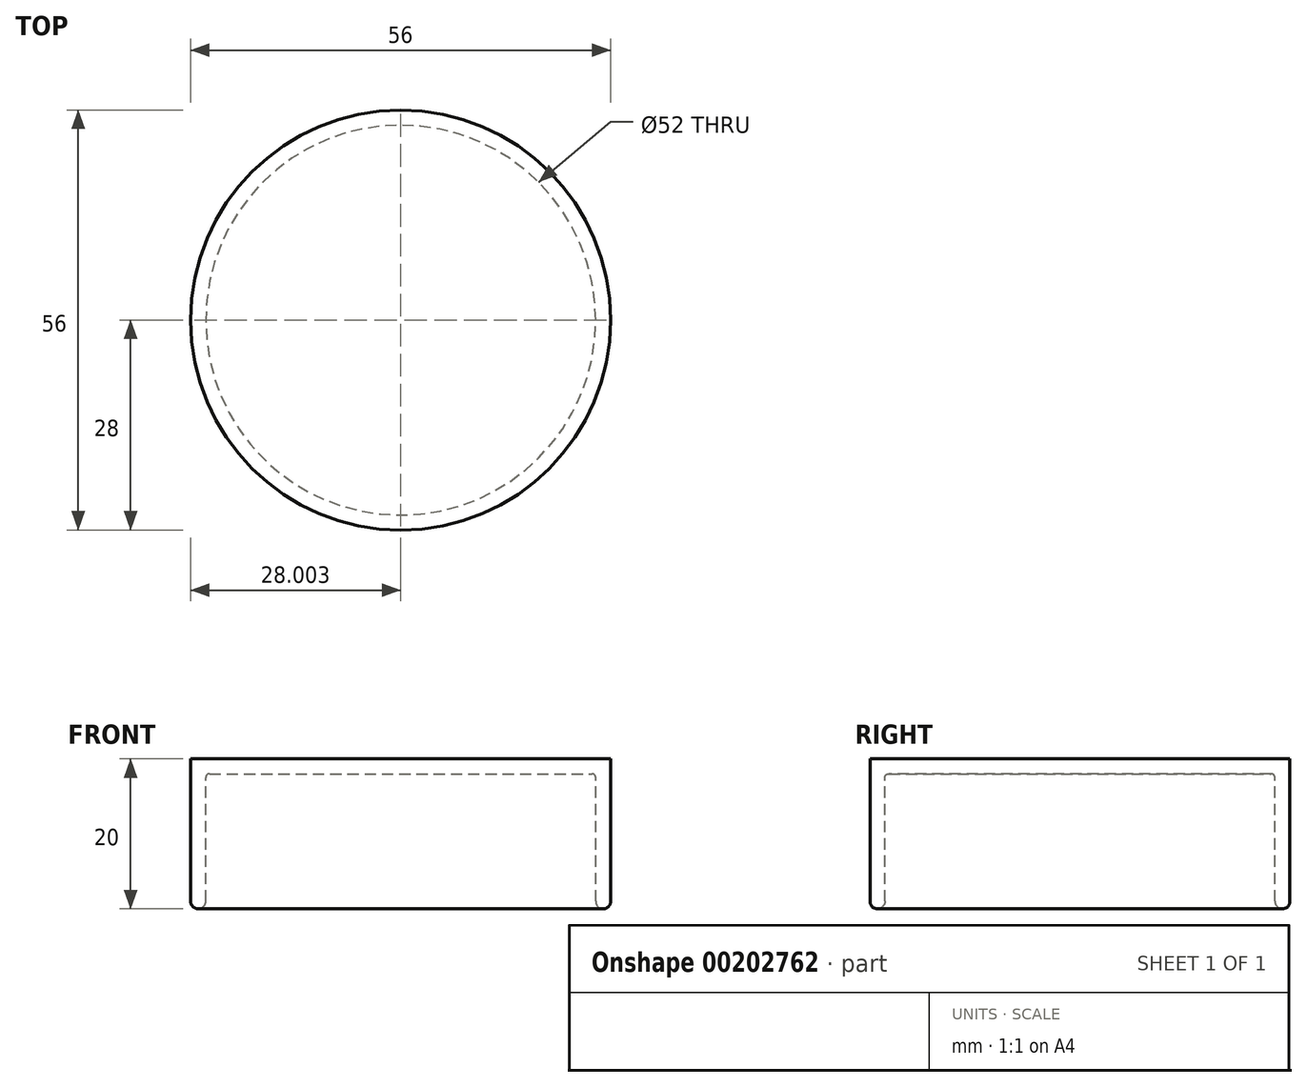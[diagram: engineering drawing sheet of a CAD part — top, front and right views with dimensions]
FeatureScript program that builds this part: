
annotation { "Feature Type Name" : "Feature", "Feature Type Description" : "" }
export const myFeature = defineFeature(function(context is Context, id is Id, definition is map)
    precondition{}
    {
        {
            var Q0;
            Q0=qCreatedBy(makeId("Front.planeOp"),FACE);
            var sketch = newSketch(context, id + "F0", { "sketchPlane" : qUnion([Q0])});
            skLineSegment(sketch, "E0.bottom", {"start": v(-8.82, 16.52) * mm, "end": v(19.18, 16.52) * mm});
            skLineSegment(sketch, "E0.top", {"start": v(-8.82, -3.48) * mm, "end": v(-6.82, -3.48) * mm});
            skLineSegment(sketch, "E0.left", {"start": v(-8.82, 16.52) * mm, "end": v(-8.82, -3.48) * mm});
            skLineSegment(sketch, "E0.right", {"start": v(19.18, 16.52) * mm, "end": v(19.18, 14.52) * mm});
            skLineSegment(sketch, "E1.0", {"start": v(-6.82, 14.52) * mm, "end": v(19.18, 14.52) * mm});
            skLineSegment(sketch, "E1.1", {"start": v(-6.82, 14.52) * mm, "end": v(-6.82, -3.48) * mm});
            skSolve(sketch);
        }
        {
            var Q0;
            Q0=makeQuery(id+"F0.imprint","IMPRINT",FACE,{"disambiguationData":[TD([[makeQuery(id+"F0.imprint","IMPRINT",EDGE,{"derivedFrom":sQuery(id+"F0.wireOp",EDGE,"E0.bottom")}),-1.0]])]});
            var Q1;
            Q1=sQuery(id+"F0.wireOp",EDGE,"E0.right");
            revolve(context, id + "F1", {"entities" : qUnion([Q0]), "axis" : qUnion([Q1]), "revolveType" : RevolveType.FULL});
        }
        {
            var Q0;
            Q0=makeQuery(id+"F1.opRevolve","SWEPT_FACE",FACE,{"disambiguationData":[OSD([sQuery(id+"F0.wireOp",EDGE,"E0.top")])]});
            fillet(context, id + "F2", {"entities" : qUnion([Q0]), "radius" : 1 * mm, "tangentPropagation" : true, "allowEdgeOverflow" : false});
        }
        {
            var Q0;
            Q0=makeQuery(id+"F1.opRevolve","SWEPT_EDGE",EDGE,{"disambiguationData":[OSD([sQuery(id+"F0.wireOp",EDGE,"E1.0"),sQuery(id+"F0.wireOp",EDGE,"E1.1")])]});
            fillet(context, id + "F3", {"entities" : qUnion([Q0]), "radius" : 0.5 * mm, "tangentPropagation" : true, "allowEdgeOverflow" : false});
        }
    });
